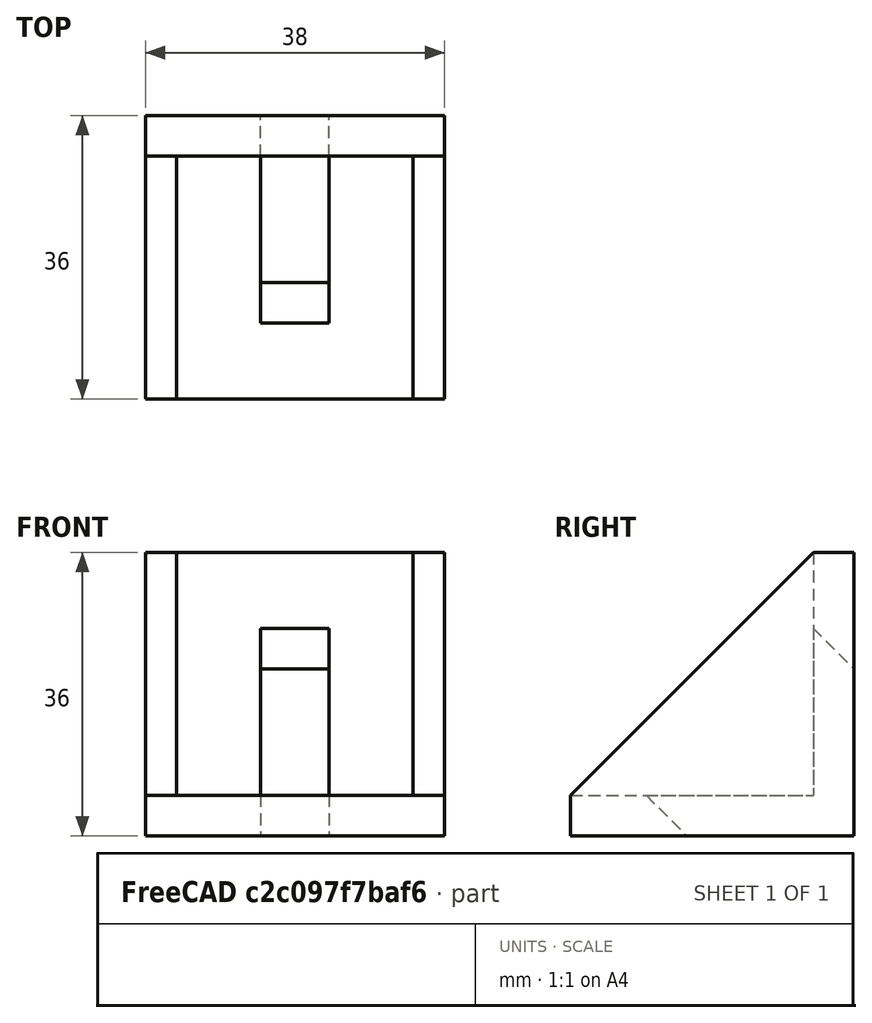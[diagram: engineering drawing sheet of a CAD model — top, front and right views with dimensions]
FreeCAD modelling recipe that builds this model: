
FCSTD DOCUMENT  (FreeCAD 1.0R39319 (Git))
Label: equerre
License: All rights reserved
LicenseURL: https://en.wikipedia.org/wiki/All_rights_reserved
objects: Sketcher::SketchObject×3, PartDesign::Pocket×2, PartDesign::Pad×1, PartDesign::Body×1, Assembly::JointGroup×1, Assembly::AssemblyObject×1
note: 16 computed .brp shape members not serialized (recipe doc carries the construction recipe); baked Part::Feature solids carry a one-line shape summary decoded from their .brp

FEATURE [Sketcher::SketchObject] Sketch
  ArcFitTolerance = 1e-06
  AttachmentSupport = -> [YZ_Plane]
  FullyConstrained = true
  MakeInternals = false
  MapMode = 5
  Placement = pos=(0,0,0) rot=(0.57735,0.57735,0.57735;2.0944rad)
  sketch-geometry (5):
    g0: LineSegment StartX=0 StartY=0 StartZ=0 EndX=-36 EndY=0 EndZ=0
    g1: LineSegment StartX=0 StartY=36 StartZ=0 EndX=0 EndY=0 EndZ=0
    g2: LineSegment StartX=-36 StartY=0 StartZ=0 EndX=-36 EndY=5.15361 EndZ=0
    g3: LineSegment StartX=0 StartY=36 StartZ=0 EndX=-5.15361 EndY=36 EndZ=0
    g4: LineSegment StartX=-36 StartY=5.15361 StartZ=0 EndX=-5.15361 EndY=36 EndZ=0
  constraints (14):
    c: Coincident(g-1,g0)
    c: PointOnObject(g0,g-1)
    c: PointOnObject(g1,g-2)
    c: Coincident(g1,g0)
    c: Equal(g1,g0)
    c: DistanceX(g0,g0) = 36
    c: Coincident(g2,g0)
    c: Coincident(g3,g1)
    c: Perpendicular(g-2,g3)
    c: Perpendicular(g-1,g2)
    c: Coincident(g4,g2)
    c: Coincident(g4,g3)
    c: Distance(g0,g4) = 29.1
    c: Equal(g2,g3)
FEATURE [PartDesign::Pad] Pad
  Direction = (1,0,0)
  Length = 38
  Length2 = 10
  Midplane = true
  Placement = pos=(0,0,0) rot=(1,1,1;2.0944rad)
  Profile = -> Sketch
  ReferenceAxis = -> Sketch [N_Axis]
  Refine = true
  Suppressed = false
  Type = 0
FEATURE [Sketcher::SketchObject] Sketch001
  ArcFitTolerance = 1e-06
  AttachmentSupport = -> [Pad]
  ExternalGeometry = -> [Pad]
  FullyConstrained = true
  MakeInternals = false
  MapMode = 5
  Placement = pos=(-19,0,0) rot=(0.57735,0.57735,-0.57735;4.18879rad)
  sketch-geometry (3):
    g0: LineSegment StartX=-36 StartY=-5.15361 StartZ=0 EndX=-5.15361 EndY=-5.15361 EndZ=0
    g1: LineSegment StartX=-5.15361 StartY=-36 StartZ=0 EndX=-5.15361 EndY=-5.15361 EndZ=0
    g2: LineSegment StartX=-5.15361 StartY=-36 StartZ=0 EndX=-36 EndY=-5.15361 EndZ=0
  constraints (7):
    c: Coincident(g0,g-5)
    c: Coincident(g1,g-5)
    c: Coincident(g1,g0)
    c: Coincident(g2,g1)
    c: Coincident(g2,g0)
    c: Perpendicular(g1,g0)
    c: Perpendicular(g1,g-6)
FEATURE [PartDesign::Pocket] Pocket
  BaseFeature = -> Pad
  Direction = (1,0,0)
  Length = 34
  Length2 = -4
  Placement = pos=(0,0,0) rot=(1,1,1;2.0944rad)
  Profile = -> Sketch001
  ReferenceAxis = -> Sketch001 [N_Axis]
  Refine = true
  Suppressed = false
  Type = 4
FEATURE [Sketcher::SketchObject] Sketch002
  ArcFitTolerance = 1e-06
  AttachmentSupport = -> [Pocket]
  ExternalGeometry = -> [Pocket]
  FullyConstrained = true
  MakeInternals = false
  MapMode = 5
  Placement = pos=(-4.7e-15,-20.5768,20.5768) rot=(0.357407,0.357407,-0.862856;1.71777rad)
  sketch-geometry (4):
    g0: LineSegment StartX=-15 StartY=4.35 StartZ=0 EndX=-15 EndY=-4.35 EndZ=0
    g1: LineSegment StartX=-15 StartY=-4.35 StartZ=0 EndX=15 EndY=-4.35 EndZ=0
    g2: LineSegment StartX=15 StartY=-4.35 StartZ=0 EndX=15 EndY=4.35 EndZ=0
    g3: LineSegment StartX=15 StartY=4.35 StartZ=0 EndX=-15 EndY=4.35 EndZ=0
  constraints (10):
    c: Coincident(g0,g1)
    c: Coincident(g1,g2)
    c: Coincident(g2,g3)
    c: Coincident(g3,g0)
    c: Vertical(g2)
    c: Horizontal(g1)
    c: Symmetric(g0,g2,g-2)
    c: Symmetric(g0,g0,g-1)
    c: DistanceY(g0,g0) = 8.7
    c: DistanceX(g3,g3) = 30
FEATURE [PartDesign::Pocket] Pocket001
  BaseFeature = -> Pocket
  Direction = (1e-16,0.707107,-0.707107)
  Length = 5
  Length2 = 5
  Placement = pos=(0,0,0) rot=(1,1,1;2.0944rad)
  Profile = -> Sketch002
  ReferenceAxis = -> Sketch002 [N_Axis]
  Refine = true
  Suppressed = false
  Type = 1
FEATURE [PartDesign::Body] Body  label="Corps"
  AllowCompound = false
  Group = -> [Sketch,Pad,Sketch001,Pocket,Sketch002,Pocket001]
  Origin = -> Origin
  Tip = -> Pocket001
FEATURE [Assembly::JointGroup] Joints
FEATURE [Assembly::AssemblyObject] Assembly
  Group = -> [Joints]
  Origin = -> Origin001
  Type = Assembly
